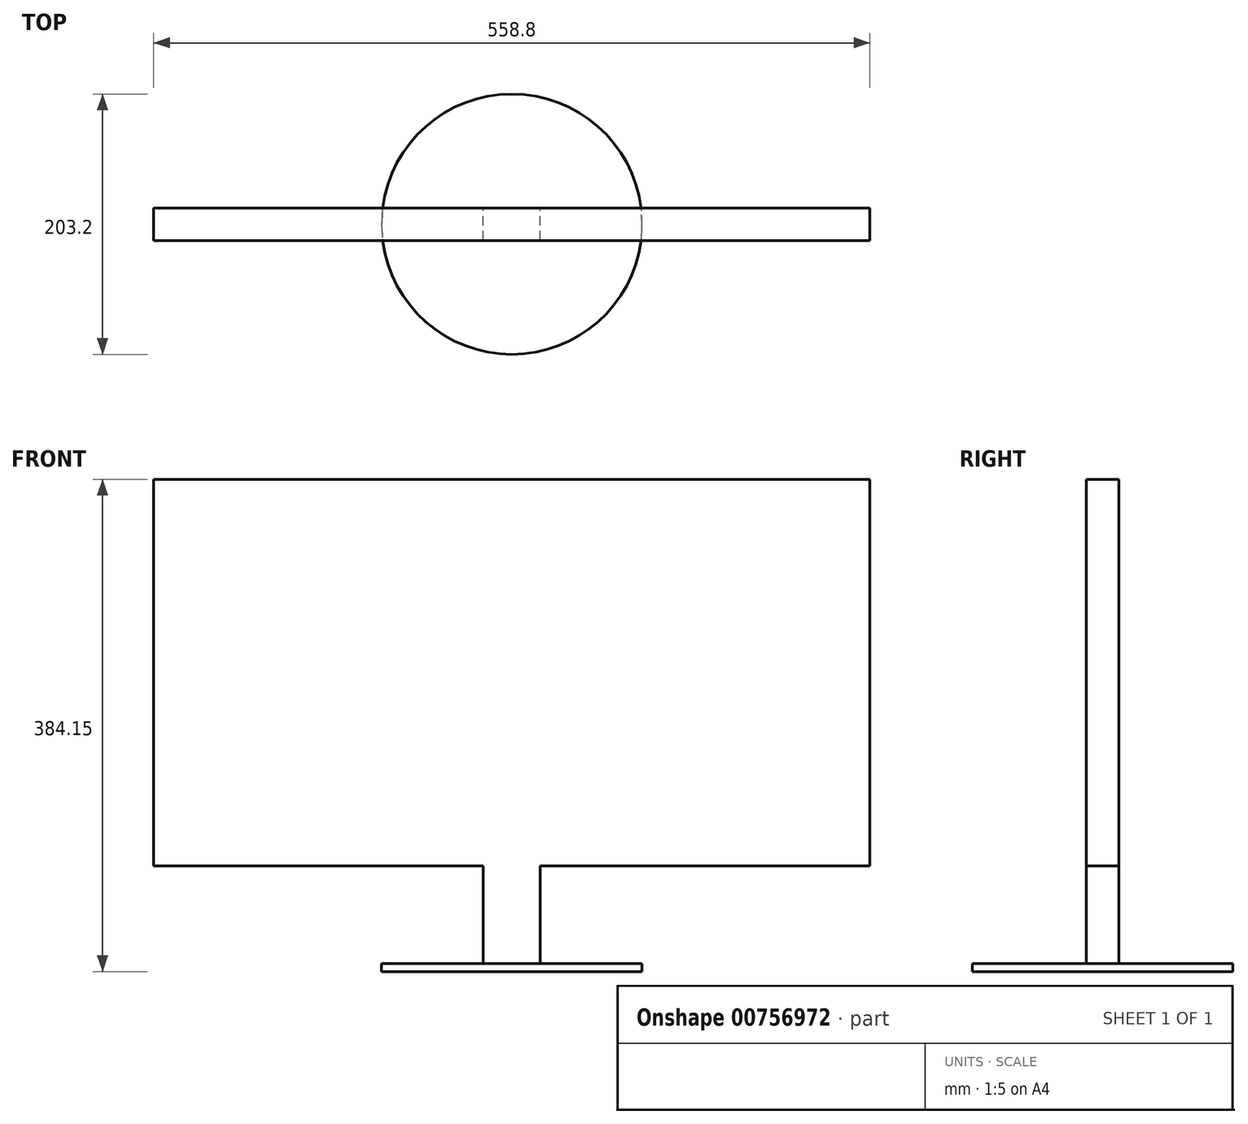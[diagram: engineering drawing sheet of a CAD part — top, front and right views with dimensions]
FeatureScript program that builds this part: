
annotation { "Feature Type Name" : "Feature", "Feature Type Description" : "" }
export const myFeature = defineFeature(function(context is Context, id is Id, definition is map)
    precondition{}
    {
        {
            var Q0;
            Q0=qCreatedBy(makeId("Front.planeOp"),FACE);
            var sketch = newSketch(context, id + "F0", { "sketchPlane" : qUnion([Q0])});
            skLineSegment(sketch, "E0.bottom", {"start": v(279.4, 150.8) * mm, "end": v(-279.4, 150.8) * mm});
            skLineSegment(sketch, "E0.top", {"start": v(279.4, -150.8) * mm, "end": v(-279.4, -150.8) * mm});
            skLineSegment(sketch, "E0.left", {"start": v(279.4, 150.8) * mm, "end": v(279.4, -150.8) * mm});
            skLineSegment(sketch, "E0.right", {"start": v(-279.4, 150.8) * mm, "end": v(-279.4, -150.8) * mm});
            skPoint(sketch, "E0.middle", {"position": v(0, 0) * mm});
            skLineSegment(sketch, "E1", {"start": v(-279.4, 150.8) * mm, "end": v(279.4, -150.8) * mm});
            skLineSegment(sketch, "E2.top", {"start": v(22.23, -227) * mm, "end": v(-22.22, -227) * mm});
            skLineSegment(sketch, "E2.left", {"start": v(22.23, -150.8) * mm, "end": v(22.23, -227) * mm});
            skLineSegment(sketch, "E2.right", {"start": v(-22.22, -150.8) * mm, "end": v(-22.22, -227) * mm});
            skPoint(sketch, "E2.middle", {"position": v(0, -150.8) * mm});
            skSolve(sketch);
        }
        {
            var Q0;
            Q0=qSketchRegion(id+"F0",true);
            extrude(context, id + "F1", {"entities" : qUnion([Q0]), "endBound" : BoundingType.SYMMETRIC, "depth" : 25.4 * mm});
        }
        {
            var Q0;
            Q0=makeQuery(id+"F1.opExtrude","SWEPT_FACE",FACE,{"disambiguationData":[OSD([sQuery(id+"F0.wireOp",EDGE,"E2.top")])]});
            var sketch = newSketch(context, id + "F2", { "sketchPlane" : qUnion([Q0])});
            skCircle(sketch, "E3", {"center": v(0, 0) * mm, "radius": 101.6 * mm});
            skSolve(sketch);
        }
        {
            var Q0;
            Q0=qSketchRegion(id+"F2",true);
            extrude(context, id + "F3", {"entities" : qUnion([Q0]), "operationType" : NewBodyOperationType.ADD, "depth" : 6.35 * mm});
        }
    });
